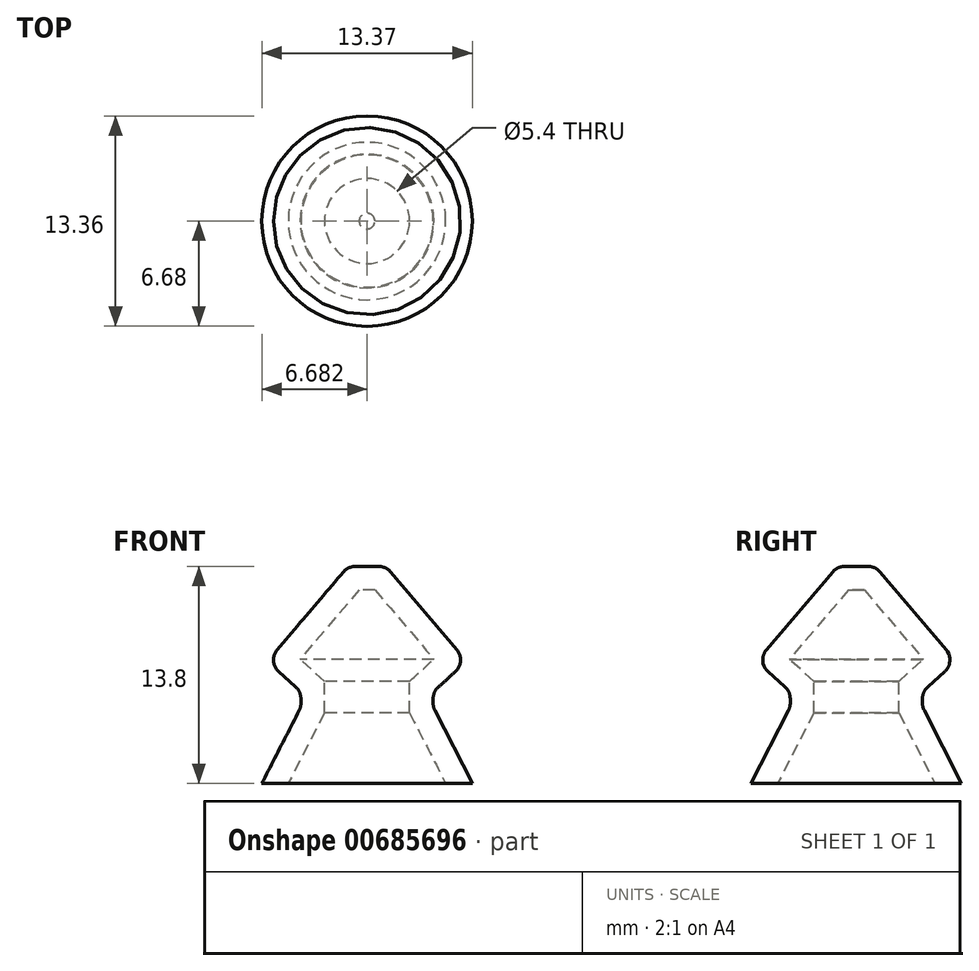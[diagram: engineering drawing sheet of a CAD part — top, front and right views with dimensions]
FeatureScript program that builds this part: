
annotation { "Feature Type Name" : "Feature", "Feature Type Description" : "" }
export const myFeature = defineFeature(function(context is Context, id is Id, definition is map)
    precondition{}
    {
        {
            var Q0;
            Q0=qCreatedBy(makeId("Front.planeOp"),FACE);
            var sketch = newSketch(context, id + "F0", { "sketchPlane" : qUnion([Q0])});
            skLineSegment(sketch, "E0", {"start": v(6.31, 4.4) * mm, "end": v(10.06, 0) * mm});
            skLineSegment(sketch, "E1", {"start": v(1.56, 0) * mm, "end": v(5.31, 4.4) * mm});
            skLineSegment(sketch, "E2", {"start": v(5.31, 4.4) * mm, "end": v(6.31, 4.4) * mm});
            skLineSegment(sketch, "E3", {"start": v(3.11, -1.4) * mm, "end": v(3.11, -3.4) * mm});
            skLineSegment(sketch, "E4", {"start": v(1.56, 0) * mm, "end": v(3.11, -1.4) * mm});
            skLineSegment(sketch, "E5", {"start": v(10.06, 0) * mm, "end": v(8.51, -1.4) * mm});
            skLineSegment(sketch, "E6", {"start": v(8.51, -1.4) * mm, "end": v(8.51, -3.4) * mm});
            skLineSegment(sketch, "E7", {"start": v(3.11, -3.4) * mm, "end": v(0.81, -7.9) * mm});
            skLineSegment(sketch, "E8", {"start": v(8.51, -3.4) * mm, "end": v(10.81, -7.9) * mm});
            skLineSegment(sketch, "E9.0", {"start": v(1.61, -3.04) * mm, "end": v(-0.87, -7.9) * mm});
            skLineSegment(sketch, "E10.0", {"start": v(1.61, -2.07) * mm, "end": v(1.61, -3.04) * mm});
            skLineSegment(sketch, "E11.0", {"start": v(-0.53, -0.14) * mm, "end": v(1.61, -2.07) * mm});
            skLineSegment(sketch, "E12.0", {"start": v(-0.53, -0.14) * mm, "end": v(4.62, 5.9) * mm});
            skLineSegment(sketch, "E13.0", {"start": v(4.62, 5.9) * mm, "end": v(7, 5.9) * mm});
            skLineSegment(sketch, "E14.0", {"start": v(7, 5.9) * mm, "end": v(12.15, -0.14) * mm});
            skLineSegment(sketch, "E15.0", {"start": v(12.15, -0.14) * mm, "end": v(10.01, -2.07) * mm});
            skLineSegment(sketch, "E16.0", {"start": v(10.01, -2.07) * mm, "end": v(10.01, -3.04) * mm});
            skLineSegment(sketch, "E17.0", {"start": v(10.01, -3.04) * mm, "end": v(12.5, -7.9) * mm});
            skLineSegment(sketch, "E18", {"start": v(10.81, -7.9) * mm, "end": v(12.5, -7.9) * mm});
            skLineSegment(sketch, "E19", {"start": v(0.81, -7.9) * mm, "end": v(-0.87, -7.9) * mm});
            skLineSegment(sketch, "E20", {"start": v(5.81, 5.9) * mm, "end": v(5.81, -2.01) * mm});
            skSolve(sketch);
        }
        {
            var Q0;
            {var subQ4=sQuery(id+"F0.wireOp",EDGE,"E1");Q0=makeQuery(id+"F0.imprint","IMPRINT",FACE,{"disambiguationData":[TD([[makeQuery(id+"F0.imprint","IMPRINT",EDGE,{"derivedFrom":subQ4}),1.0]])]});}
            var Q1;
            Q1=sQuery(id+"F0.wireOp",EDGE,"E20");
            revolve(context, id + "F1", {"entities" : qUnion([Q0]), "axis" : qUnion([Q1]), "revolveType" : RevolveType.FULL});
        }
        {
            var Q0;
            Q0=makeQuery(id+"F1.opRevolve","SWEPT_EDGE",EDGE,{"disambiguationData":[OSD([sQuery(id+"F0.wireOp",EDGE,"E11.0"),sQuery(id+"F0.wireOp",EDGE,"E12.0")])]});
            var Q1;
            Q1=makeQuery(id+"F1.opRevolve","SWEPT_EDGE",EDGE,{"disambiguationData":[OSD([sQuery(id+"F0.wireOp",EDGE,"E12.0"),sQuery(id+"F0.wireOp",EDGE,"E13.0")])]});
            var Q2;
            Q2=makeQuery(id+"F1.opRevolve","SWEPT_EDGE",EDGE,{"disambiguationData":[OSD([sQuery(id+"F0.wireOp",EDGE,"E10.0"),sQuery(id+"F0.wireOp",EDGE,"E11.0")])]});
            var Q3;
            Q3=makeQuery(id+"F1.opRevolve","SWEPT_EDGE",EDGE,{"disambiguationData":[OSD([sQuery(id+"F0.wireOp",EDGE,"E9.0"),sQuery(id+"F0.wireOp",EDGE,"E10.0")])]});
            fillet(context, id + "F2", {"entities" : qUnion([Q0, Q1, Q2, Q3]), "radius" : 1 * mm, "tangentPropagation" : true, "allowEdgeOverflow" : false});
        }
    });
